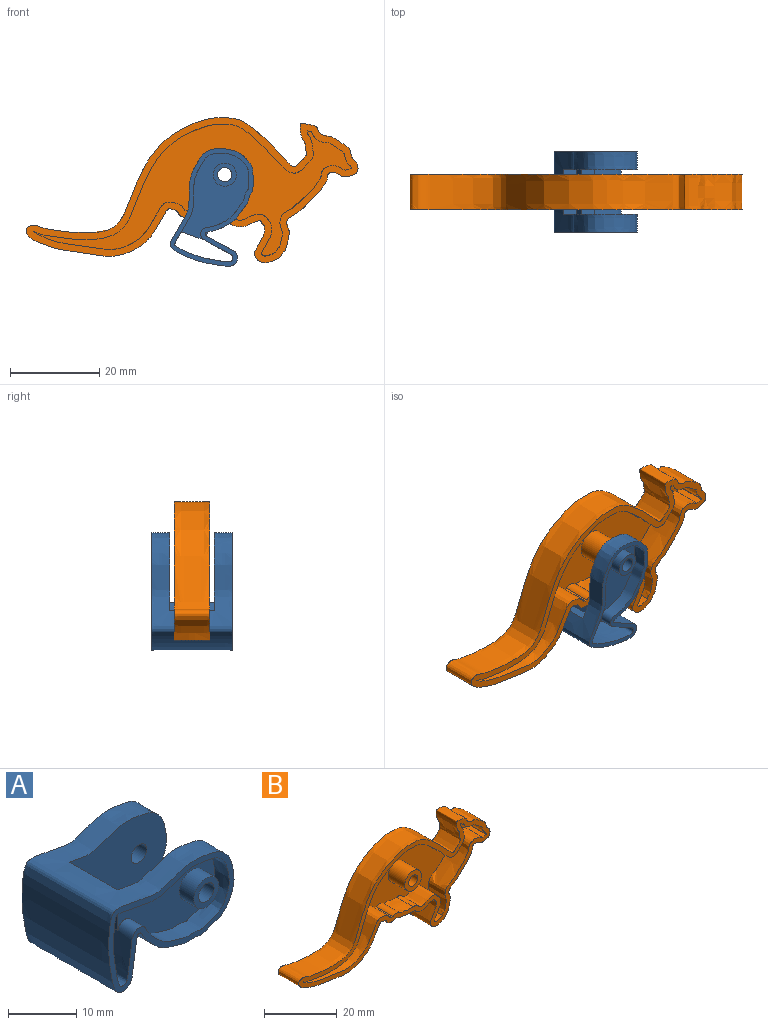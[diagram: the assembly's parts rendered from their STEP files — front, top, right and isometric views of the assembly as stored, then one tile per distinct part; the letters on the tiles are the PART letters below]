
ASSEMBLY  parts=2 mates=1
PART A: 21 faces, bbox 28.9x20.8x19 mm
  f0: plane 10x3.1mm, normal (1,0,0), area 31mm2, adj f1,f6,f9,f16
  f1: plane 20.18x14.12mm, normal (0,1,0), area 204.3mm2, adj f0,f6,f8,f16,f18,f20
  f2: plane 26.16x16.31mm, normal (0,-1,0), area 78.7mm2, adj f6,f10
  f3: plane 5.2x5.2mm, normal (0,-1,0), area 13.2mm2, adj f8,f12
  f4: plane 26.16x16.31mm, normal (0,1,0), area 78.7mm2, adj f6,f10
  f5: plane 5.2x5.2mm, normal (0,1,0), area 13.2mm2, adj f7,f11
  f6: extruded ~25.96x18mm, area 954.2mm2, adj f0,f1,f2,f4,f9,f17,f18,f19
  f7: cylinder r=1.6mm len=4mm, axis (0,1,0), area 40.2mm2, adj f5,f9
  f8: cylinder r=1.6mm len=4mm, axis (0,1,0), area 40.2mm2, adj f1,f3
  f9: plane 20.18x14.12mm, normal (0,-1,0), area 204.3mm2, adj f0,f6,f7,f16,f18,f20
  f10: extruded ~24x18mm, area 738.5mm2, adj f2,f4,f13,f14,f15
  f11: cylinder r=2.6mm len=5.2mm, axis (0,1,0), area 49mm2, adj f5,f13
  f12: cylinder r=2.6mm len=5.2mm, axis (0,1,0), area 49mm2, adj f3,f15
  f13: plane 22.91x14.86mm, normal (0,1,0), area 155.6mm2, adj f10,f11,f14
  f14: plane 12.08x5.5mm, normal (-1,0,0), area 65mm2, adj f10,f13,f15
  f15: plane 22.91x14.86mm, normal (0,-1,0), area 155.6mm2, adj f10,f12,f14
  f16: plane 10x3mm, normal (0,0,1), area 30mm2, adj f0,f1,f9,f20
  f17: plane 1.01x0.42mm, normal (0,-1,0), area 0.3mm2, adj f6,f18
  f18: plane 10x3mm, normal (0,0,-1), area 30mm2, adj f1,f6,f9,f17,f19,f20
  f19: plane 1.01x0.42mm, normal (0,1,0), area 0.3mm2, adj f6,f18
  f20: plane 10x3.29mm, normal (1,0,0), area 32.9mm2, adj f1,f9,f16,f18
PART B: 22 faces, bbox 79.7x12.7x37.7 mm
  f0: plane 79.66x37.71mm, normal (0,-1,0), area 393mm2, adj f2,f5,f6,f7,f8,f9,f10,f11
  f1: plane 6.5x6.5mm, normal (0,-1,0), area 23.6mm2, adj f3,f20
  f2: extruded ~72.7x32.27mm, area 1669.9mm2, adj f0,f4
  f3: cylinder r=1.75mm len=8mm, axis (0,1,0), area 88mm2, adj f1,f4
  f4: plane 74.94x32.99mm, normal (0,1,0), area 1090.2mm2, adj f2,f3
  f5: extruded ~62.53x25.79mm, area 561mm2, adj f0,f6,f19,f21
  f6: extruded ~33.86x10.58mm, area 256.7mm2, adj f0,f5,f7,f21
  f7: extruded ~6.5x0.59mm, area 4mm2, adj f0,f6,f8,f21
  f8: extruded ~6.5x0.51mm, area 3.4mm2, adj f0,f7,f9,f21
  f9: extruded ~6.5x2.8mm, area 19.8mm2, adj f0,f8,f10,f21
  f10: extruded ~6.5x5.12mm, area 33.7mm2, adj f0,f9,f11,f21
  f11: extruded ~6.5x2.17mm, area 17.2mm2, adj f0,f10,f12,f21
  f12: extruded ~7.3x6.5mm, area 52.2mm2, adj f0,f11,f13,f21
  f13: extruded ~7.79x6.5mm, area 56.2mm2, adj f0,f12,f14,f21
  f14: extruded ~6.5x3.16mm, area 22.9mm2, adj f0,f13,f15,f21
  f15: extruded ~19.44x15.68mm, area 191.5mm2, adj f0,f14,f16,f21
  f16: extruded ~6.5x1.37mm, area 9.3mm2, adj f0,f15,f17,f21
  f17: extruded ~6.5x5.79mm, area 52.8mm2, adj f0,f16,f18,f21
  f18: extruded ~6.5x3.89mm, area 32.2mm2, adj f0,f17,f19,f21
  f19: extruded ~6.5x0.95mm, area 6.4mm2, adj f0,f5,f18,f21
  f20: cylinder r=3.25mm len=6.5mm, axis (0,1,0), area 132.7mm2, adj f1,f21
  f21: plane 75.96x34.23mm, normal (0,-1,0), area 673.6mm2, adj f5,f6,f7,f8,f9,f10,f11,f12
PLACE A rot(axis=(0,-1,0),70.3deg) t=(2.16,22.92,-45.4)mm
PLACE B t=(-32.97,17.92,-21.14)mm fixed
MATE revolute A.f7 <-> B.f3  axis (0,-1,0) through (15.92,18.92,23.84)mm
